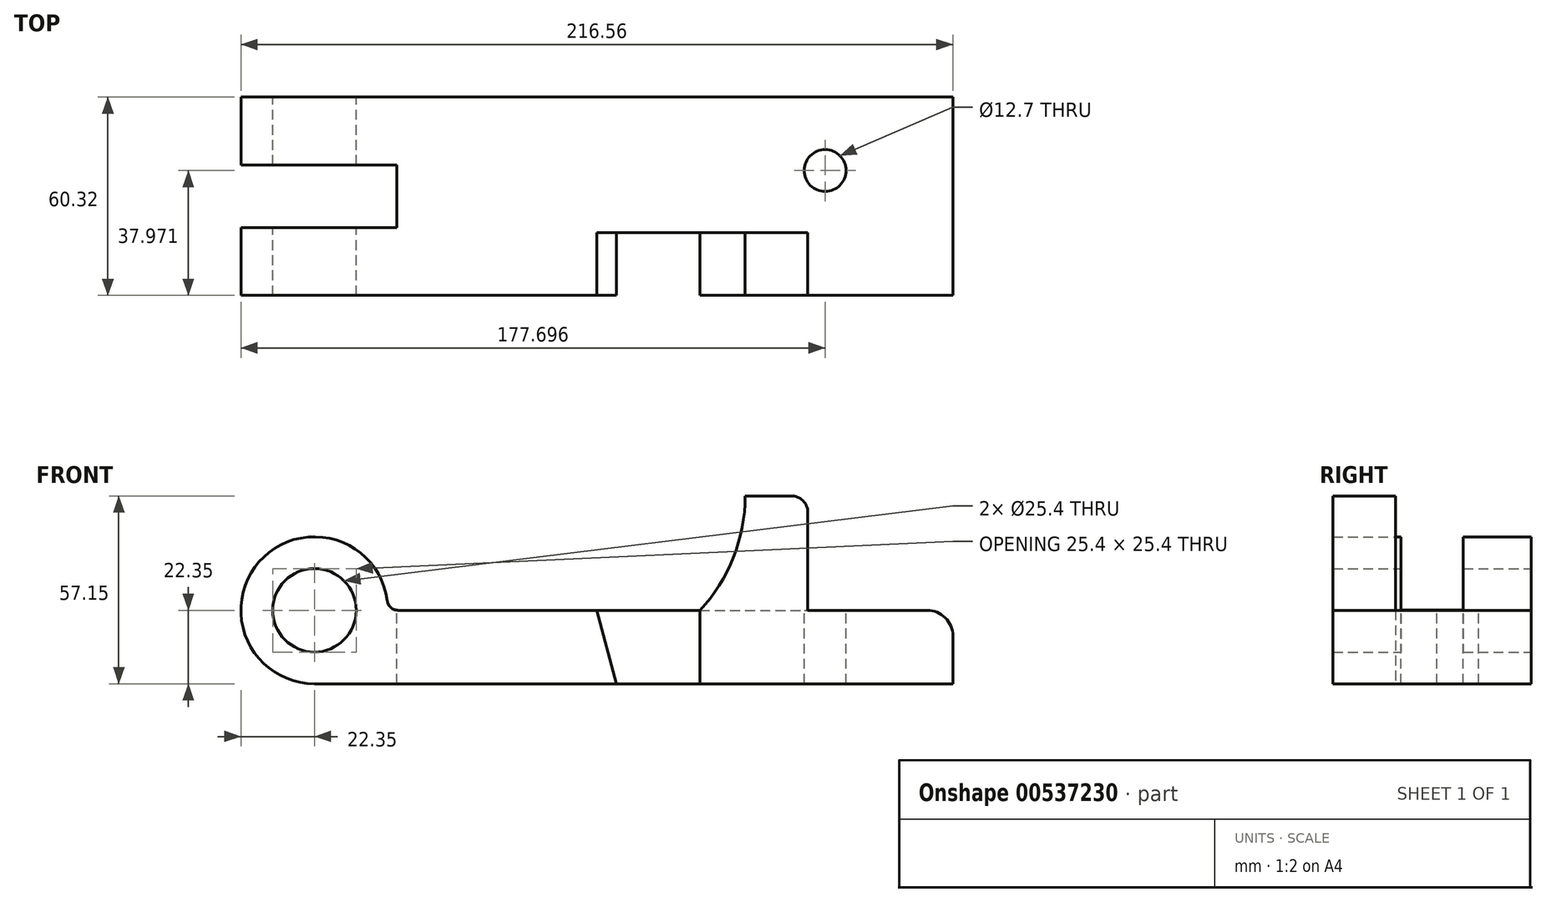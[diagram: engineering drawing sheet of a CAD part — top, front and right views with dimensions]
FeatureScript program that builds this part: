
annotation { "Feature Type Name" : "Feature", "Feature Type Description" : "" }
export const myFeature = defineFeature(function(context is Context, id is Id, definition is map)
    precondition{}
    {
        {
            var Q0;
            Q0=qCreatedBy(makeId("Front.planeOp"),FACE);
            var sketch = newSketch(context, id + "F0", { "sketchPlane" : qUnion([Q0])});
            skArc(sketch, "E0", {"start": v(22.35, 0) * mm, "mid": v(-15.8, 15.8) * mm, "end": v(0, -22.35) * mm});
            skCircle(sketch, "E1", {"center": v(0, 0) * mm, "radius": 12.7 * mm});
            skLineSegment(sketch, "E2.top", {"start": v(0, -22.35) * mm, "end": v(194.2, -22.35) * mm});
            skLineSegment(sketch, "E2.right", {"start": v(194.2, 0) * mm, "end": v(194.2, -22.35) * mm});
            skLineSegment(sketch, "E3.trimOffspring", {"start": v(22.35, 0) * mm, "end": v(194.2, 0) * mm});
            skSolve(sketch);
        }
        {
            var Q0;
            Q0=makeQuery(id+"F0.imprint","IMPRINT",FACE,{"disambiguationData":[TD([[makeQuery(id+"F0.imprint","IMPRINT",EDGE,{"derivedFrom":sQuery(id+"F0.wireOp",EDGE,"E0")}),1.0]])]});
            extrude(context, id + "F1", {"entities" : qUnion([Q0]), "depth" : 60.32 * mm, "offsetDistance" : 25.4 * mm, "symmetric" : true});
        }
        {
            var Q0;
            Q0=qCreatedBy(makeId("Top.planeOp"),FACE);
            var sketch = newSketch(context, id + "F2", { "sketchPlane" : qUnion([Q0])});
            skLineSegment(sketch, "E4.bottom", {"start": v(25, 9.5) * mm, "end": v(-25, 9.5) * mm});
            skLineSegment(sketch, "E4.top", {"start": v(25, -9.5) * mm, "end": v(-25, -9.5) * mm});
            skLineSegment(sketch, "E4.left", {"start": v(25, 9.5) * mm, "end": v(25, -9.5) * mm});
            skLineSegment(sketch, "E4.right", {"start": v(-25, 9.5) * mm, "end": v(-25, -9.5) * mm});
            skPoint(sketch, "E4.middle", {"position": v(0, 0) * mm});
            skCircle(sketch, "E5", {"center": v(155.35, 7.81) * mm, "radius": 6.35 * mm});
            skSolve(sketch);
        }
        {
            var Q0;
            Q0=makeQuery(id+"F2.imprint","IMPRINT",FACE,{"disambiguationData":[TD([[makeQuery(id+"F2.imprint","IMPRINT",EDGE,{"derivedFrom":sQuery(id+"F2.wireOp",EDGE,"E5")}),1.0]])]});
            var Q1;
            Q1=makeQuery(id+"F2.imprint","IMPRINT",FACE,{"disambiguationData":[TD([[makeQuery(id+"F2.imprint","IMPRINT",EDGE,{"derivedFrom":sQuery(id+"F2.wireOp",EDGE,"E4.bottom")}),1.0]])]});
            extrude(context, id + "F3", {"entities" : qUnion([Q0, Q1]), "operationType" : NewBodyOperationType.REMOVE, "endBound" : BoundingType.THROUGH_ALL, "oppositeDirection" : true, "depth" : 25.4 * mm, "offsetDistance" : 25.4 * mm, "hasSecondDirection" : true, "secondDirectionOppositeDirection" : false, "secondDirectionDepth" : 25.4 * mm});
        }
        {
            var Q0;
            Q0=makeQuery(id+"F1.opExtrude","CAP_FACE",FACE,{"disambiguationData":[OSD([sQuery(id+"F0.wireOp",EDGE,"E0"),sQuery(id+"F0.wireOp",EDGE,"E1"),sQuery(id+"F0.wireOp",EDGE,"E2.top"),sQuery(id+"F0.wireOp",EDGE,"E2.right"),sQuery(id+"F0.wireOp",EDGE,"E3.trimOffspring")])],"isStart":false});
            var sketch = newSketch(context, id + "F4", { "sketchPlane" : qUnion([Q0])});
            skLineSegment(sketch, "E6", {"start": v(117.25, 0) * mm, "end": v(117.25, -22.35) * mm});
            skLineSegment(sketch, "E7", {"start": v(117.25, -22.35) * mm, "end": v(91.85, -22.35) * mm});
            skLineSegment(sketch, "E8", {"start": v(91.85, -22.35) * mm, "end": v(85.85, 0) * mm});
            skLineSegment(sketch, "E9", {"start": v(85.85, 0) * mm, "end": v(117.25, 0) * mm});
            skSolve(sketch);
        }
        {
            var Q0;
            Q0=makeQuery(id+"F4.imprint","IMPRINT",FACE,{"disambiguationData":[TD([[makeQuery(id+"F4.imprint","IMPRINT",EDGE,{"derivedFrom":sQuery(id+"F4.wireOp",EDGE,"E6")}),-1.0]])]});
            extrude(context, id + "F5", {"entities" : qUnion([Q0]), "operationType" : NewBodyOperationType.REMOVE, "oppositeDirection" : true, "depth" : 19.05 * mm, "offsetDistance" : 25.4 * mm});
        }
        {
            var Q0;
            {var subQ0=sQuery(id+"F0.wireOp",EDGE,"E2.top");var subQ1=sQuery(id+"F0.wireOp",EDGE,"E2.right");var subQ2=sQuery(id+"F0.wireOp",EDGE,"E3.trimOffspring");Q0=makeQuery(id+"F5.boolean.opBoolean","SPLIT",FACE,{"disambiguationData":[TD([makeQuery(id+"F1.opExtrude","SWEPT_FACE",FACE,{"disambiguationData":[OSD([subQ1])]})])],"derivedFrom":makeQuery(id+"F1.opExtrude","CAP_FACE",FACE,{"disambiguationData":[OSD([sQuery(id+"F0.wireOp",EDGE,"E0"),sQuery(id+"F0.wireOp",EDGE,"E1"),subQ0,subQ1,subQ2])],"isStart":false})});}
            var sketch = newSketch(context, id + "F6", { "sketchPlane" : qUnion([Q0])});
            skLineSegment(sketch, "E10", {"start": v(150.09, 0) * mm, "end": v(150.09, 34.8) * mm});
            skLineSegment(sketch, "E11", {"start": v(150.09, 34.8) * mm, "end": v(131.04, 34.8) * mm});
            skArc(sketch, "E12", {"start": v(117.25, 0) * mm, "mid": v(127.46, 16.08) * mm, "end": v(131.04, 34.8) * mm});
            skSolve(sketch);
        }
        {
            var Q0;
            {var subQ0=sQuery(id+"F6.wireOp",EDGE,"E10");Q0=makeQuery(id+"F6.imprint","IMPRINT",FACE,{"disambiguationData":[TD([[makeQuery(id+"F6.imprint","IMPRINT",EDGE,{"derivedFrom":subQ0}),1.0]])]});}
            extrude(context, id + "F7", {"entities" : qUnion([Q0]), "operationType" : NewBodyOperationType.ADD, "oppositeDirection" : true, "depth" : 19.05 * mm, "offsetDistance" : 25.4 * mm});
        }
        {
            var Q0;
            Q0=makeQuery(id+"F7.opExtrude","SWEPT_EDGE",EDGE,{"disambiguationData":[OSD([sQuery(id+"F6.wireOp",EDGE,"E10"),sQuery(id+"F6.wireOp",EDGE,"E11")])]});
            fillet(context, id + "F8", {"entities" : qUnion([Q0]), "radius" : 5.08 * mm, "tangentPropagation" : true, "allowEdgeOverflow" : false});
        }
        {
            var Q0;
            Q0=makeQuery(id+"F1.opExtrude","SWEPT_EDGE",EDGE,{"disambiguationData":[OSD([sQuery(id+"F0.wireOp",EDGE,"E2.right"),sQuery(id+"F0.wireOp",EDGE,"E3.trimOffspring")])]});
            fillet(context, id + "F9", {"entities" : qUnion([Q0]), "radius" : 7.87 * mm, "tangentPropagation" : true, "allowEdgeOverflow" : false});
        }
        {
            var Q0;
            {var subQ0=sQuery(id+"F0.wireOp",EDGE,"E0");var subQ1=sQuery(id+"F0.wireOp",EDGE,"E3.trimOffspring");Q0=makeQuery(id+"F3.boolean.opBoolean","SPLIT",EDGE,{"disambiguationData":[TD([makeQuery(id+"F3.opExtrude","SWEPT_FACE",FACE,{"disambiguationData":[OSD([sQuery(id+"F2.wireOp",EDGE,"E4.top")])]})])],"derivedFrom":makeQuery(id+"F1.opExtrude","SWEPT_EDGE",EDGE,{"disambiguationData":[OSD([subQ0,subQ1])]})});}
            fillet(context, id + "F10", {"entities" : qUnion([Q0]), "radius" : 3.3 * mm, "tangentPropagation" : true, "allowEdgeOverflow" : false});
        }
    });
